FCSTD DOCUMENT  (FreeCAD 0.20R29177 +426 (Git))
Label: proj_1
License: All rights reserved
LicenseURL: https://en.wikipedia.org/wiki/All_rights_reserved
objects: Sketcher::SketchObject×1, PartDesign::Body×1
note: 2 computed .brp shape members not serialized (recipe doc carries the construction recipe); baked Part::Feature solids carry a one-line shape summary decoded from their .brp

FEATURE [Sketcher::SketchObject] Sketch
  FullyConstrained = true
  MapMode = 5
  Support = -> [XY_Plane]
  sketch-geometry (45):
    g0: Circle CenterX=0 CenterY=0 CenterZ=0 NormalX=0 NormalY=0 NormalZ=1 AngleXU=0 Radius=100
    g1: GeomPoint X=0 Y=0 Z=0
    g2: GeomPoint X=0 Y=0 Z=0
    g3: LineSegment StartX=173.205 StartY=100 StartZ=0 EndX=173.205 EndY=200 EndZ=0
    g4: LineSegment StartX=173.205 StartY=200 StartZ=0 EndX=86.6025 EndY=250 EndZ=0
    g5: LineSegment StartX=86.6025 StartY=250 StartZ=0 EndX=0 EndY=200 EndZ=0
    g6: LineSegment StartX=0 StartY=200 StartZ=0 EndX=0 EndY=100 EndZ=0
    g7: LineSegment StartX=0 StartY=100 StartZ=0 EndX=86.6025 EndY=50 EndZ=0
    g8: LineSegment StartX=86.6025 StartY=50 StartZ=0 EndX=173.205 EndY=100 EndZ=0
    g9: Circle CenterX=86.6025 CenterY=150 CenterZ=0 NormalX=0 NormalY=0 NormalZ=1 AngleXU=0 Radius=100
    g10: LineSegment StartX=-86.6025 StartY=50 StartZ=0 EndX=0 EndY=100 EndZ=0
    g11: LineSegment StartX=0 StartY=100 StartZ=0 EndX=-8e-16 EndY=200 EndZ=0
    g12: LineSegment StartX=-8e-16 StartY=200 StartZ=0 EndX=-86.6025 EndY=250 EndZ=0
    g13: LineSegment StartX=-86.6025 StartY=250 StartZ=0 EndX=-173.205 EndY=200 EndZ=0
    g14: LineSegment StartX=-173.205 StartY=200 StartZ=0 EndX=-173.205 EndY=100 EndZ=0
    g15: Circle CenterX=-86.6025 CenterY=150 CenterZ=0 NormalX=0 NormalY=0 NormalZ=1 AngleXU=0 Radius=100
    g16: LineSegment StartX=259.808 StartY=-50 StartZ=0 EndX=259.808 EndY=50 EndZ=0
    g17: LineSegment StartX=259.808 StartY=50 StartZ=0 EndX=173.205 EndY=100 EndZ=0
    g18: LineSegment StartX=173.205 StartY=100 StartZ=0 EndX=86.6025 EndY=50 EndZ=0
    g19: LineSegment StartX=86.6025 StartY=50 StartZ=0 EndX=86.6025 EndY=-50 EndZ=0
    g20: LineSegment StartX=86.6025 StartY=-50 StartZ=0 EndX=173.205 EndY=-100 EndZ=0
    g21: LineSegment StartX=173.205 StartY=-100 StartZ=0 EndX=259.808 EndY=-50 EndZ=0
    g22: Circle CenterX=173.205 CenterY=-1.7e-15 CenterZ=0 NormalX=0 NormalY=0 NormalZ=1 AngleXU=0 Radius=100
    g23: LineSegment StartX=173.205 StartY=-200 StartZ=0 EndX=173.205 EndY=-100 EndZ=0
    g24: LineSegment StartX=173.205 StartY=-100 StartZ=0 EndX=86.6025 EndY=-50 EndZ=0
    g25: LineSegment StartX=86.6025 StartY=-50 StartZ=0 EndX=0 EndY=-100 EndZ=0
    g26: LineSegment StartX=0 StartY=-100 StartZ=0 EndX=3.9e-15 EndY=-200 EndZ=0
    g27: LineSegment StartX=3.9e-15 StartY=-200 StartZ=0 EndX=86.6025 EndY=-250 EndZ=0
    g28: LineSegment StartX=86.6025 StartY=-250 StartZ=0 EndX=173.205 EndY=-200 EndZ=0
    g29: Circle CenterX=86.6025 CenterY=-150 CenterZ=0 NormalX=0 NormalY=0 NormalZ=1 AngleXU=0 Radius=100
    g30: LineSegment StartX=0 StartY=-200 StartZ=0 EndX=0 EndY=-100 EndZ=0
    g31: LineSegment StartX=0 StartY=-100 StartZ=0 EndX=-86.6025 EndY=-50 EndZ=0
    g32: LineSegment StartX=-86.6025 StartY=-50 StartZ=0 EndX=-173.205 EndY=-100 EndZ=0
    g33: LineSegment StartX=-173.205 StartY=-100 StartZ=0 EndX=-173.205 EndY=-200 EndZ=0
    g34: LineSegment StartX=-173.205 StartY=-200 StartZ=0 EndX=-86.6025 EndY=-250 EndZ=0
    g35: LineSegment StartX=-86.6025 StartY=-250 StartZ=0 EndX=0 EndY=-200 EndZ=0
    g36: Circle CenterX=-86.6025 CenterY=-150 CenterZ=0 NormalX=0 NormalY=0 NormalZ=1 AngleXU=0 Radius=100
    g37: LineSegment StartX=-86.6025 StartY=-50 StartZ=0 EndX=-86.6025 EndY=50 EndZ=0
    g38: LineSegment StartX=-86.6025 StartY=50 StartZ=0 EndX=-173.205 EndY=100 EndZ=0
    g39: LineSegment StartX=-173.205 StartY=100 StartZ=0 EndX=-259.808 EndY=50 EndZ=0
    g40: LineSegment StartX=-259.808 StartY=50 StartZ=0 EndX=-259.808 EndY=-50 EndZ=0
    g41: LineSegment StartX=-259.808 StartY=-50 StartZ=0 EndX=-173.205 EndY=-100 EndZ=0
    g42: LineSegment StartX=-173.205 StartY=-100 StartZ=0 EndX=-86.6025 EndY=-50 EndZ=0
    g43: Circle CenterX=-173.205 CenterY=-4.3e-15 CenterZ=0 NormalX=0 NormalY=0 NormalZ=1 AngleXU=0 Radius=100
    g44: LineSegment StartX=-173.205 StartY=100 StartZ=0 EndX=-86.6025 EndY=50 EndZ=0
  constraints (100):
    c: PointOnObject(g18,g0)
    c: PointOnObject(g6,g0)
    c: PointOnObject(g10,g0)
    c: PointOnObject(g31,g0)
    c: PointOnObject(g25,g0)
    c: PointOnObject(g19,g0)
    c: Coincident(g0,g-1)
    c: PointOnObject(g25,g-2)
    c: DistanceY(g19,g18) = 100
    c: Coincident(g1,g0)
    c: Coincident(g2,g0)
    c: Coincident(g3,g4)
    c: Coincident(g4,g5)
    c: Coincident(g5,g6)
    c: Coincident(g6,g7)
    c: Coincident(g7,g8)
    c: Coincident(g8,g3)
    c: Equal(g3, g4-g8) x5
    c: PointOnObject(g3,g9)
    c: PointOnObject(g4,g9)
    c: PointOnObject(g5,g9)
    c: PointOnObject(g6,g9)
    c: PointOnObject(g7,g9)
    c: PointOnObject(g8,g9)
    c: Coincident(g10,g11)
    c: Coincident(g11,g12)
    c: Coincident(g12,g13)
    c: Coincident(g13,g14)
    c: Equal(g10, g11-g14) x4
    c: PointOnObject(g10,g15)
    c: PointOnObject(g11,g15)
    c: PointOnObject(g12,g15)
    c: PointOnObject(g13,g15)
    c: PointOnObject(g14,g15)
    c: PointOnObject(g10,g15)
    c: Coincident(g16,g17)
    c: Coincident(g17,g18)
    c: Coincident(g18,g19)
    c: Coincident(g19,g20)
    c: Coincident(g20,g21)
    c: Coincident(g21,g16)
    c: Equal(g16, g17-g21) x5
    c: PointOnObject(g16,g22)
    c: PointOnObject(g17,g22)
    c: PointOnObject(g18,g22)
    c: PointOnObject(g19,g22)
    c: PointOnObject(g20,g22)
    c: PointOnObject(g21,g22)
    c: Coincident(g23,g24)
    c: Coincident(g24,g25)
    c: Coincident(g25,g26)
    c: Coincident(g26,g27)
    c: Coincident(g27,g28)
    c: Coincident(g28,g23)
    c: Equal(g23, g24-g28) x5
    c: PointOnObject(g23,g29)
    c: PointOnObject(g24,g29)
    c: PointOnObject(g25,g29)
    c: PointOnObject(g26,g29)
    c: PointOnObject(g27,g29)
    c: PointOnObject(g28,g29)
    c: Coincident(g30,g31)
    c: Coincident(g31,g32)
    c: Coincident(g32,g33)
    c: Coincident(g33,g34)
    c: Coincident(g34,g35)
    c: Coincident(g35,g30)
    c: Equal(g30, g31-g35) x5
    c: PointOnObject(g30,g36)
    c: PointOnObject(g31,g36)
    c: PointOnObject(g32,g36)
    c: PointOnObject(g33,g36)
    c: PointOnObject(g34,g36)
    c: PointOnObject(g35,g36)
    c: Coincident(g37,g38)
    c: Coincident(g38,g39)
    c: Coincident(g39,g40)
    c: Coincident(g40,g41)
    c: Coincident(g41,g42)
    c: Coincident(g42,g37)
    c: Equal(g37, g38-g42) x5
    c: PointOnObject(g37,g43)
    c: PointOnObject(g38,g43)
    c: PointOnObject(g39,g43)
    c: PointOnObject(g40,g43)
    c: PointOnObject(g41,g43)
    c: PointOnObject(g42,g43)
    c: Coincident(g7,g18)
    c: Coincident(g25,g30)
    c: Coincident(g31,g37)
    c: Coincident(g10,g37)
    c: Coincident(g6,g10)
    c: Coincident(g19,g24)
    c: Equal(g37,g10)
    c: Equal(g10,g7)
    c: Equal(g7,g19)
    c: Equal(g19,g25)
    c: Coincident(g14,g38)
    c: Coincident(g44,g14)
    c: Coincident(g44,g10)
FEATURE [PartDesign::Body] Body
  Group = -> [Sketch]
  Origin = -> Origin
